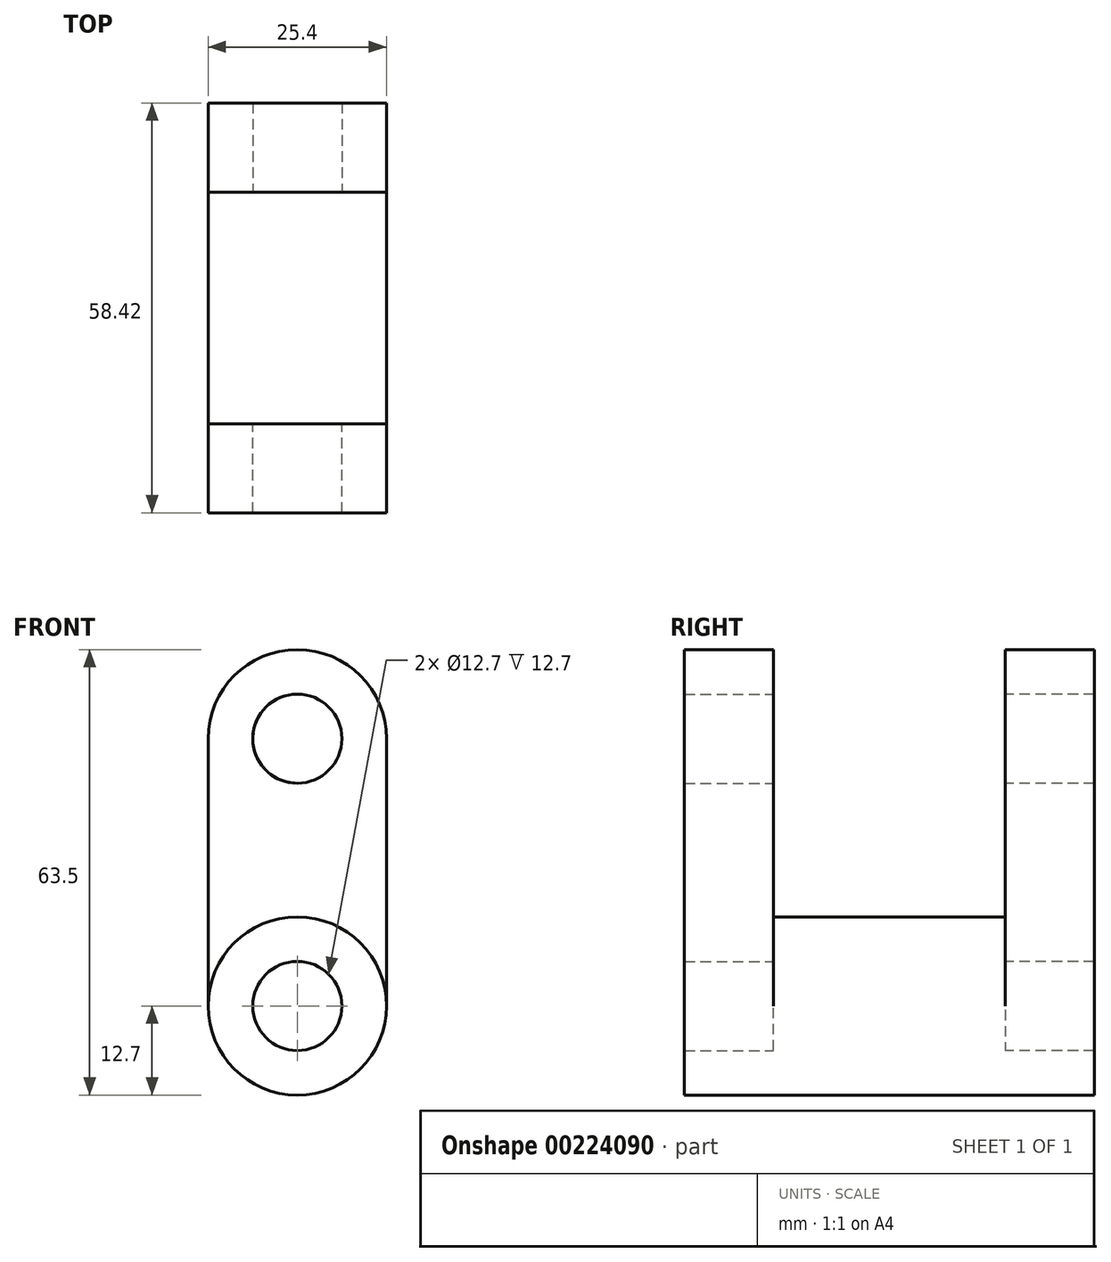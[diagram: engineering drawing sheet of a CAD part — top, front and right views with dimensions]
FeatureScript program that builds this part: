
annotation { "Feature Type Name" : "Feature", "Feature Type Description" : "" }
export const myFeature = defineFeature(function(context is Context, id is Id, definition is map)
    precondition{}
    {
        {
            var Q0;
            Q0=qCreatedBy(makeId("Front.planeOp"),FACE);
            var sketch = newSketch(context, id + "F0", { "sketchPlane" : qUnion([Q0])});
            skCircle(sketch, "E0", {"center": v(0, 0) * mm, "radius": 12.7 * mm});
            skSolve(sketch);
        }
        {
            var Q0;
            Q0 = qSketchRegion(id + "F0", true);
            extrude(context, id + "F1", {"entities" : qUnion([Q0]), "endBound" : BoundingType.SYMMETRIC, "oppositeDirection" : true, "depth" : 33.02 * mm});
        }
        {
            var Q0;
            Q0=makeQuery(id+"F1.opExtrude","CAP_FACE",FACE,{"disambiguationData":[OSD([sQuery(id+"F0.wireOp",EDGE,"E0")])],"isStart":true});
            var sketch = newSketch(context, id + "F2", { "sketchPlane" : qUnion([Q0])});
            skLineSegment(sketch, "E1.left", {"start": v(12.7, 38.1) * mm, "end": v(12.7, 0) * mm});
            skLineSegment(sketch, "E1.right", {"start": v(-12.7, 38.1) * mm, "end": v(-12.7, 0) * mm});
            skPoint(sketch, "E1.middle", {"position": v(0, 19.05) * mm});
            skArc(sketch, "E2", {"start": v(12.7, 38.1) * mm, "mid": v(0, 50.8) * mm, "end": v(-12.7, 38.1) * mm});
            skCircle(sketch, "E3", {"center": v(0, 38.1) * mm, "radius": 6.35 * mm});
            skCircle(sketch, "E4.MirrorC", {"center": v(0, 0) * mm, "radius": 6.35 * mm});
            skArc(sketch, "E5", {"start": v(-12.7, 0) * mm, "mid": v(0, -12.7) * mm, "end": v(12.7, 0) * mm});
            skSolve(sketch);
        }
        {
            var Q0;
            Q0 = qSketchRegion(id + "F2", true);
            extrude(context, id + "F3", {"entities" : qUnion([Q0]), "operationType" : NewBodyOperationType.ADD, "depth" : 12.7 * mm});
        }
        {
            var Q0;
            Q0=makeQuery(id+"F1.opExtrude","CAP_FACE",FACE,{"disambiguationData":[OSD([sQuery(id+"F0.wireOp",EDGE,"E0")])],"isStart":false});
            var sketch = newSketch(context, id + "F4", { "sketchPlane" : qUnion([Q0])});
            skLineSegment(sketch, "E6.left", {"start": v(12.7, 38.1) * mm, "end": v(12.7, 0) * mm});
            skLineSegment(sketch, "E6.right", {"start": v(-12.7, 38.1) * mm, "end": v(-12.7, 0) * mm});
            skPoint(sketch, "E6.middle", {"position": v(0, 19.05) * mm});
            skArc(sketch, "E7", {"start": v(12.7, 38.1) * mm, "mid": v(0, 50.8) * mm, "end": v(-12.7, 38.1) * mm});
            skCircle(sketch, "E8", {"center": v(0, 38.1) * mm, "radius": 6.35 * mm});
            skCircle(sketch, "E9.MirrorC", {"center": v(0, 0) * mm, "radius": 6.35 * mm});
            skArc(sketch, "E10", {"start": v(-12.7, 0) * mm, "mid": v(0, -12.7) * mm, "end": v(12.7, 0) * mm});
            skSolve(sketch);
        }
        {
            var Q0;
            Q0 = qSketchRegion(id + "F4", true);
            extrude(context, id + "F5", {"entities" : qUnion([Q0]), "operationType" : NewBodyOperationType.ADD, "depth" : 12.7 * mm});
        }
    });
